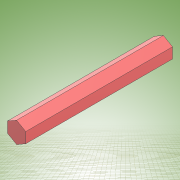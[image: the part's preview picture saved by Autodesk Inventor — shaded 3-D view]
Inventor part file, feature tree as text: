
AUTODESK INVENTOR PART (.ipt)
format: ipt  version: 2022 (Build 260153000, 153)  size: 117,760 bytes
history: native  units: mm
features: other x1, extrude x1, sketch x1
ambient origin geometry x8: Origin, YZ Plane, XZ Plane, XY Plane, X Axis, Y Axis, Z Axis, Center Point
bodies: Body1 (feature_tree)
feature tree (3):
  other  "Sólido1"
  extrude  "Extrusión1"  Depth=45.0mm TaperAngle=0.0deg
  sketch  "Boceto1"  dims[d0=5.6mm d1=45.0mm d2=0.0mm]
